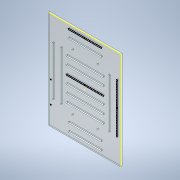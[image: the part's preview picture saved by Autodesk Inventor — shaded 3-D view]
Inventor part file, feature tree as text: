
AUTODESK INVENTOR PART (.ipt)
format: ipt  version: 2021 (Build 250183000, 183)  size: 221,184 bytes
history: native  units: mm
features: other x9, extrude x4, sketch x4, pattern_linear x3, hole x2, pattern_circular x1
ambient origin geometry x8: Origin, YZ Plane, XZ Plane, XY Plane, X Axis, Y Axis, Z Axis, Center Point
bodies: Body1 (feature_tree)
feature tree (23):
  other  "Sólido1"
  extrude  "Extrusão1"  Depth=242.0mm
  hole  "Furo1"  [1 undecoded]
  sketch  "Esboço3"  dims[d4=3.0mm d5=42.0mm d6=4.0mm d7=2.0mm d8=90.0deg d9=8.0mm d10=0.0mm d11=80.0mm]
  extrude  "Extrusão2"  Depth=120.0mm
  extrude  "Extrusão4"  Depth=3.0mm
  extrude  "Extrusão5"  Depth=10.0mm
  pattern_linear  "Padrão retangular1"  Count1=9  [1 undecoded]
  pattern_linear  "Padrão retangular2"  Spacing1=3.0mm  [1 undecoded]
  pattern_linear  "Padrão retangular3"  Spacing1=10.0mm  [1 undecoded]
  pattern_circular  "Padrão circular1"  Count=11  [1 undecoded]
  hole  "Furo2"  [1 undecoded]
  sketch  "Esboço1"  dims[d0=178.0mm d1=242.0mm]
  sketch  "Esboço2"  dims[d2=3.0mm d3=0.0mm]
  other  "Referência1"
  other  "Referência2"
  other  "Referência3"
  other  "Referência4"
  sketch  "Esboço4"  dims[d12=3.0mm d20=120.0mm d21=3.0mm d22=10.0mm d23=90.0mm d24=3.0mm d26=10.0mm d27=110.0mm d28=0.0mm d29=0.0mm d32=0.0mm d33=0.0mm d34=0.0mm d35=0.0mm d36=60.0mm d38=20.0mm d39=20.0mm d41=20.0mm d42=20.0mm d44=20.0mm d45=20.0mm d46=360.0deg d48=3.0mm d49=6.0mm d50=4.0mm d51=2.0mm d52=90.0deg d53=8.0mm d54=20.594885mm]
  parser-record x1  (decoder bookkeeping rows leaked as tree rows — omitted from the tree; the rows remain in map.json)
  other  "Omni Robot.iam"
  other  "chapa lentral:1"
  other  "chapa lentral:2"
note: 6 required parameter values undecoded (feature->parameter linkage not recoverable at this tier; creation-order binding heuristic only, values carry confidence <= 0.55)
note: 1 file-system path scrubbed to <path> (originals preserved in map.json)
